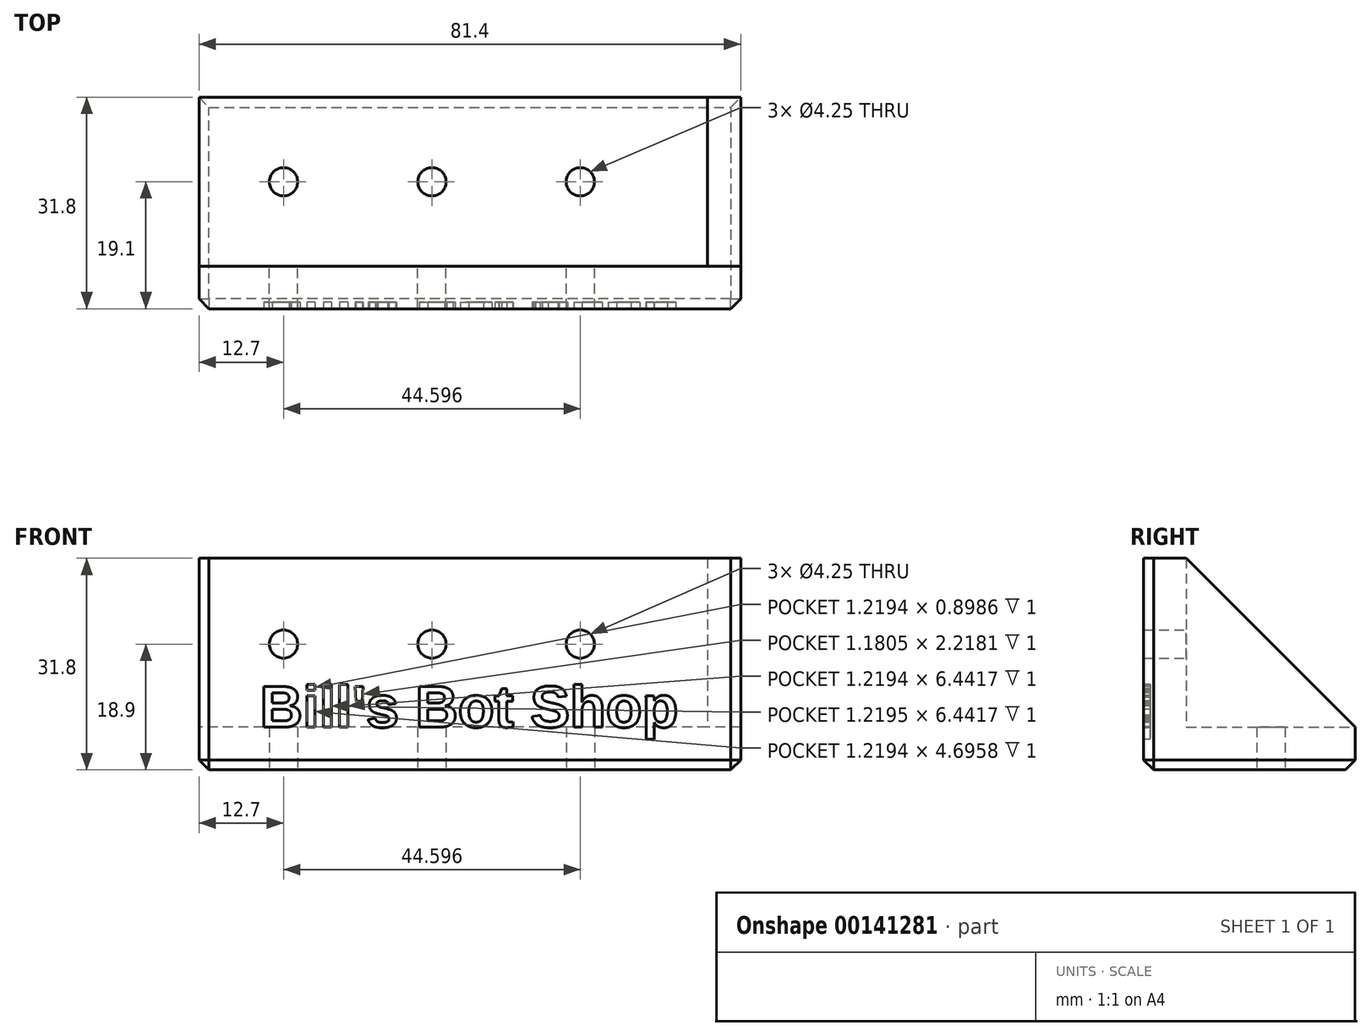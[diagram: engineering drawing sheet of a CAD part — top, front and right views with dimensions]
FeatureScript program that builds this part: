
annotation { "Feature Type Name" : "Feature", "Feature Type Description" : "" }
export const myFeature = defineFeature(function(context is Context, id is Id, definition is map)
    precondition{}
    {
        {
            var Q0;
            Q0=qCreatedBy(makeId("Top.planeOp"),FACE);
            var sketch = newSketch(context, id + "F0", { "sketchPlane" : qUnion([Q0])});
            skLineSegment(sketch, "E0.bottom", {"start": v(38.2, -12.7) * mm, "end": v(-38.2, -12.7) * mm});
            skLineSegment(sketch, "E0.top", {"start": v(38.2, 12.7) * mm, "end": v(31.8, 12.7) * mm, "construction": true});
            skLineSegment(sketch, "E0.left", {"start": v(38.2, -12.7) * mm, "end": v(38.2, 12.7) * mm});
            skLineSegment(sketch, "E0.right", {"start": v(-38.2, -12.7) * mm, "end": v(-38.2, 12.7) * mm});
            skPoint(sketch, "E0.middle", {"position": v(0, 0) * mm});
            skCircle(sketch, "E1", {"center": v(-25.5, 0) * mm, "radius": 2.12 * mm});
            skCircle(sketch, "E2.1.0.0", {"center": v(-3.2, 0) * mm, "radius": 2.12 * mm});
            skCircle(sketch, "E2.2.0.0", {"center": v(19.1, 0) * mm, "radius": 2.12 * mm});
            skLineSegment(sketch, "E2.direction1", {"start": v(-25.5, 0) * mm, "end": v(-3.2, 0) * mm, "construction": true});
            skLineSegment(sketch, "E3", {"start": v(31.8, 12.7) * mm, "end": v(31.8, -12.7) * mm, "construction": true});
            skLineSegment(sketch, "E4.trimOffspring", {"start": v(38.2, 12.7) * mm, "end": v(-38.2, 12.7) * mm});
            skSolve(sketch);
        }
        {
            var Q0;
            Q0 = qSketchRegion(id + "F0", true);
            extrude(context, id + "F1", {"entities" : qUnion([Q0]), "depth" : 6.4 * mm});
        }
        {
            var Q0;
            Q0=makeQuery(id+"F1.opExtrude","SWEPT_FACE",FACE,{"disambiguationData":[OSD([sQuery(id+"F0.wireOp",EDGE,"E0.bottom")])]});
            var sketch = newSketch(context, id + "F2", { "sketchPlane" : qUnion([Q0])});
            skLineSegment(sketch, "E5.bottom", {"start": v(38.2, 0) * mm, "end": v(-38.2, 0) * mm});
            skLineSegment(sketch, "E5.top", {"start": v(38.2, 31.8) * mm, "end": v(-38.2, 31.8) * mm});
            skLineSegment(sketch, "E5.left", {"start": v(38.2, 0) * mm, "end": v(38.2, 31.8) * mm});
            skLineSegment(sketch, "E5.right", {"start": v(-38.2, 0) * mm, "end": v(-38.2, 31.8) * mm});
            skPoint(sketch, "E5.middle", {"position": v(0, 15.9) * mm});
            skCircle(sketch, "E6", {"center": v(-25.5, 18.9) * mm, "radius": 2.12 * mm});
            skCircle(sketch, "E7.1.0.0", {"center": v(-3.2, 18.9) * mm, "radius": 2.12 * mm});
            skLineSegment(sketch, "E7.direction1", {"start": v(-25.5, 18.9) * mm, "end": v(-3.2, 18.9) * mm, "construction": true});
            skLineSegment(sketch, "E8", {"start": v(31.8, 31.8) * mm, "end": v(31.8, 0) * mm, "construction": true});
            skCircle(sketch, "E9.0.2.0", {"center": v(19.1, 18.9) * mm, "radius": 2.12 * mm});
            skSolve(sketch);
        }
        {
            var Q0;
            Q0 = qSketchRegion(id + "F2", true);
            extrude(context, id + "F3", {"entities" : qUnion([Q0]), "operationType" : NewBodyOperationType.ADD, "depth" : 6.4 * mm});
        }
        {
            var Q0;
            Q0=makeQuery(id+"F3.boolean.opBoolean","MERGE",FACE,{"derivedFrom":[makeQuery(id+"F1.opExtrude","SWEPT_FACE",FACE,{"disambiguationData":[OSD([sQuery(id+"F0.wireOp",EDGE,"E0.left")])]}),makeQuery(id+"F3.opExtrude","SWEPT_FACE",FACE,{"disambiguationData":[OSD([sQuery(id+"F2.wireOp",EDGE,"E5.left")])]})]});
            var sketch = newSketch(context, id + "F4", { "sketchPlane" : qUnion([Q0])});
            skLineSegment(sketch, "E10", {"start": v(-19.1, 31.8) * mm, "end": v(-19.1, 0) * mm});
            skLineSegment(sketch, "E11", {"start": v(-12.7, 31.8) * mm, "end": v(-19.1, 31.8) * mm});
            skLineSegment(sketch, "E12", {"start": v(-19.1, 0) * mm, "end": v(12.7, 0) * mm});
            skLineSegment(sketch, "E13", {"start": v(12.7, 0) * mm, "end": v(12.7, 6.4) * mm});
            skLineSegment(sketch, "E14", {"start": v(12.7, 6.4) * mm, "end": v(-12.7, 31.8) * mm});
            skSolve(sketch);
        }
        {
            var Q0;
            Q0 = qSketchRegion(id + "F4", true);
            extrude(context, id + "F5", {"entities" : qUnion([Q0]), "operationType" : NewBodyOperationType.ADD, "depth" : 5 * mm});
        }
        {
            var Q0;
            Q0=makeQuery(id+"F5.boolean.opBoolean","MERGE",EDGE,{"derivedFrom":[makeQuery(id+"F3.opExtrude","CAP_EDGE",EDGE,{"disambiguationData":[OSD([sQuery(id+"F2.wireOp",EDGE,"E5.bottom")])],"isStart":false}),makeQuery(id+"F5.opExtrude","SWEPT_EDGE",EDGE,{"disambiguationData":[OSD([sQuery(id+"F4.wireOp",EDGE,"E10"),sQuery(id+"F4.wireOp",EDGE,"OvD0ihgT-R2PO-Rg5G-MNsx-Zom96H0gyLIH")])]})]});
            var Q1;
            Q1=makeQuery(id+"F5.opExtrude","CAP_EDGE",EDGE,{"disambiguationData":[OSD([sQuery(id+"F4.wireOp",EDGE,"OvD0ihgT-R2PO-Rg5G-MNsx-Zom96H0gyLIH")])],"isStart":false});
            var Q2;
            Q2=makeQuery(id+"F5.opExtrude","CAP_EDGE",EDGE,{"disambiguationData":[OSD([sQuery(id+"F4.wireOp",EDGE,"E10")])],"isStart":false});
            var Q3;
            Q3=makeQuery(id+"F3.opExtrude","CAP_EDGE",EDGE,{"disambiguationData":[OSD([sQuery(id+"F2.wireOp",EDGE,"E5.right")])],"isStart":false});
            var Q4;
            Q4=makeQuery(id+"F3.boolean.opBoolean","MERGE",EDGE,{"derivedFrom":[makeQuery(id+"F1.opExtrude","CAP_EDGE",EDGE,{"disambiguationData":[OSD([sQuery(id+"F0.wireOp",EDGE,"E0.right")])],"isStart":true}),makeQuery(id+"F3.opExtrude","SWEPT_EDGE",EDGE,{"disambiguationData":[OSD([sQuery(id+"F2.wireOp",EDGE,"E5.bottom"),sQuery(id+"F2.wireOp",EDGE,"E5.right")])]})]});
            var Q5;
            Q5=makeQuery(id+"F1.opExtrude","CAP_EDGE",EDGE,{"disambiguationData":[OSD([sQuery(id+"F0.wireOp",EDGE,"E4.trimOffspring")])],"isStart":true});
            var Q6;
            Q6=makeQuery(id+"F1.opExtrude","CAP_EDGE",EDGE,{"disambiguationData":[OSD([sQuery(id+"F0.wireOp",EDGE,"OXAnvrdN-1jBS-4D07-qUoH-0s5XSjywuS0s")])],"isStart":true});
            var Q7;
            Q7=makeQuery(id+"F5.opExtrude","CAP_EDGE",EDGE,{"disambiguationData":[OSD([sQuery(id+"F4.wireOp",EDGE,"400knlT5-wIwl-FGyO-LaSt-zxC5BG6yE1My")])],"isStart":false});
            var Q8;
            Q8=makeQuery(id+"F5.boolean.opBoolean","MERGE",EDGE,{"derivedFrom":[makeQuery(id+"F1.opExtrude","CAP_EDGE",EDGE,{"disambiguationData":[OSD([sQuery(id+"F0.wireOp",EDGE,"91uyzQn2-5uo2-JCnp-epyX-5zE31W0V2WqM")])],"isStart":true}),makeQuery(id+"F5.opExtrude","SWEPT_EDGE",EDGE,{"disambiguationData":[OSD([sQuery(id+"F4.wireOp",EDGE,"OvD0ihgT-R2PO-Rg5G-MNsx-Zom96H0gyLIH"),sQuery(id+"F4.wireOp",EDGE,"400knlT5-wIwl-FGyO-LaSt-zxC5BG6yE1My")])]})]});
            var Q9;
            Q9=makeQuery(id+"F5.opExtrude","CAP_EDGE",EDGE,{"disambiguationData":[OSD([sQuery(id+"F4.wireOp",EDGE,"E12")])],"isStart":false});
            chamfer(context, id + "F6", {"entities" : qUnion([Q0, Q1, Q2, Q3, Q4, Q5, Q6, Q7, Q8, Q9]), "width" : 1.5 * mm, "tangentPropagation" : true});
        }
        {
            var Q0;
            Q0=makeQuery(id+"F5.boolean.opBoolean","MERGE",FACE,{"derivedFrom":[makeQuery(id+"F3.opExtrude","CAP_FACE",FACE,{"disambiguationData":[OSD([sQuery(id+"F2.wireOp",EDGE,"E5.bottom"),sQuery(id+"F2.wireOp",EDGE,"E5.top"),sQuery(id+"F2.wireOp",EDGE,"E5.left"),sQuery(id+"F2.wireOp",EDGE,"E5.right"),sQuery(id+"F2.wireOp",EDGE,"E6"),sQuery(id+"F2.wireOp",EDGE,"E7.1.0.0"),sQuery(id+"F2.wireOp",EDGE,"E9.0.2.0")])],"isStart":false}),makeQuery(id+"F5.opExtrude","SWEPT_FACE",FACE,{"disambiguationData":[OSD([sQuery(id+"F4.wireOp",EDGE,"E10")])]})]});
            var sketch = newSketch(context, id + "F7", { "sketchPlane" : qUnion([Q0])});
            skText(sketch, "E15", { "text": "Bill\'s Bot Shop", "fontName": "Arimo-Bold.ttf"});
            const initialGuessF7  = {"E15": [-0.02905, 0.0064, 1, 0, 0.0064]};
            skSetInitialGuess(sketch, initialGuessF7);
            skSolve(sketch);
        }
        {
            var Q0;
            Q0 = qSketchRegion(id + "F7", true);
            extrude(context, id + "F8", {"entities" : qUnion([Q0]), "operationType" : NewBodyOperationType.REMOVE, "oppositeDirection" : true, "depth" : 1 * mm});
        }
    });
